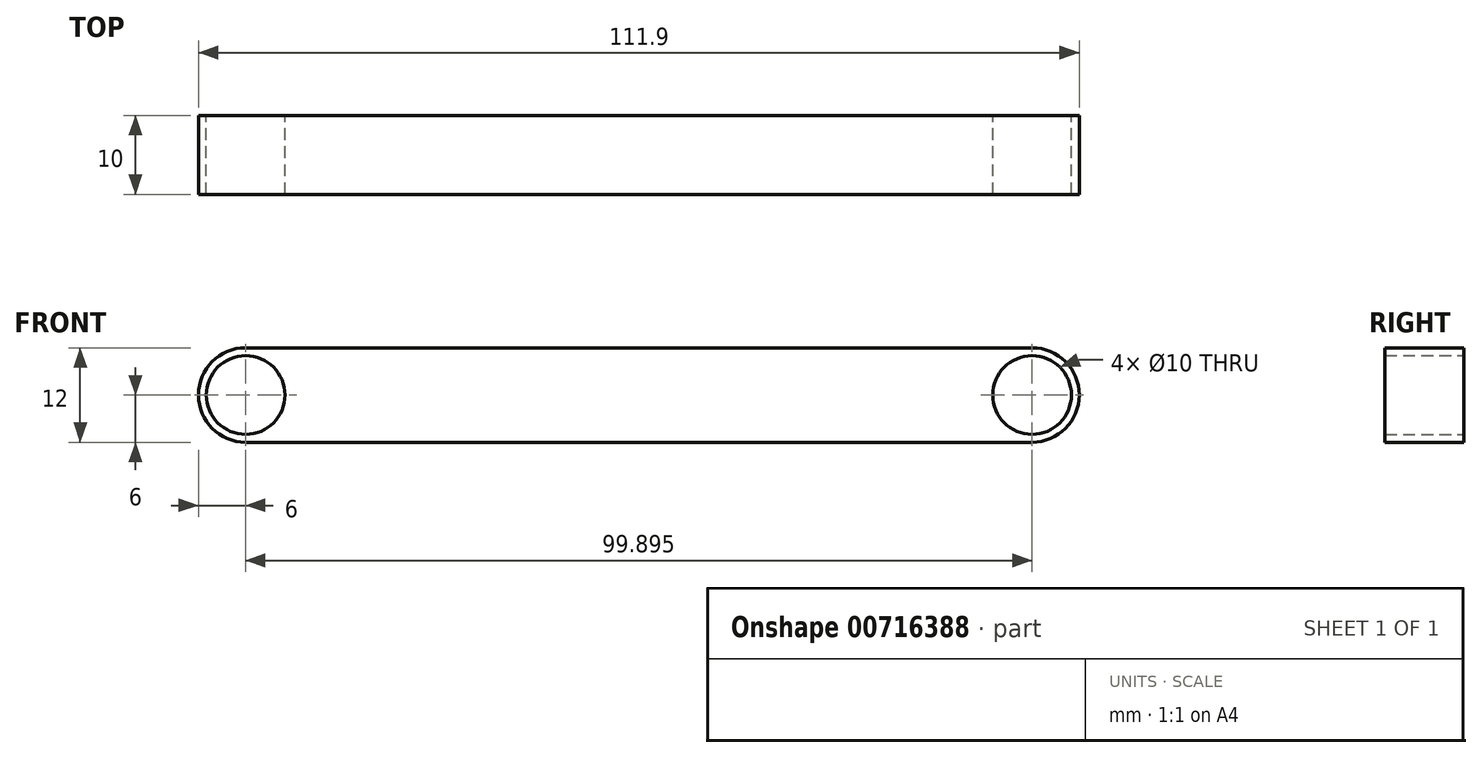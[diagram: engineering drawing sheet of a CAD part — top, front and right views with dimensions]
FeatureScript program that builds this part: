
annotation { "Feature Type Name" : "Feature", "Feature Type Description" : "" }
export const myFeature = defineFeature(function(context is Context, id is Id, definition is map)
    precondition{}
    {
        {
            var Q0;
            Q0=qCreatedBy(makeId("Front.planeOp"),FACE);
            var sketch = newSketch(context, id + "F0", { "sketchPlane" : qUnion([Q0])});
            skCircle(sketch, "E0", {"center": v(0, 0) * mm, "radius": 6 * mm});
            skLineSegment(sketch, "E1", {"start": v(0, 6) * mm, "end": v(100, 6) * mm});
            skLineSegment(sketch, "E2", {"start": v(0, -6) * mm, "end": v(100, -6) * mm});
            skCircle(sketch, "E3", {"center": v(99.9, 0) * mm, "radius": 6 * mm});
            skCircle(sketch, "E4", {"center": v(99.9, 0) * mm, "radius": 5 * mm});
            skCircle(sketch, "E5", {"center": v(0, 0) * mm, "radius": 5 * mm});
            skSolve(sketch);
        }
        {
            var Q0;
            Q0 = qSketchRegion(id + "F0", true);
            extrude(context, id + "F1", {"entities" : qUnion([Q0]), "depth" : 10 * mm, "offsetDistance" : 25 * mm});
        }
    });
